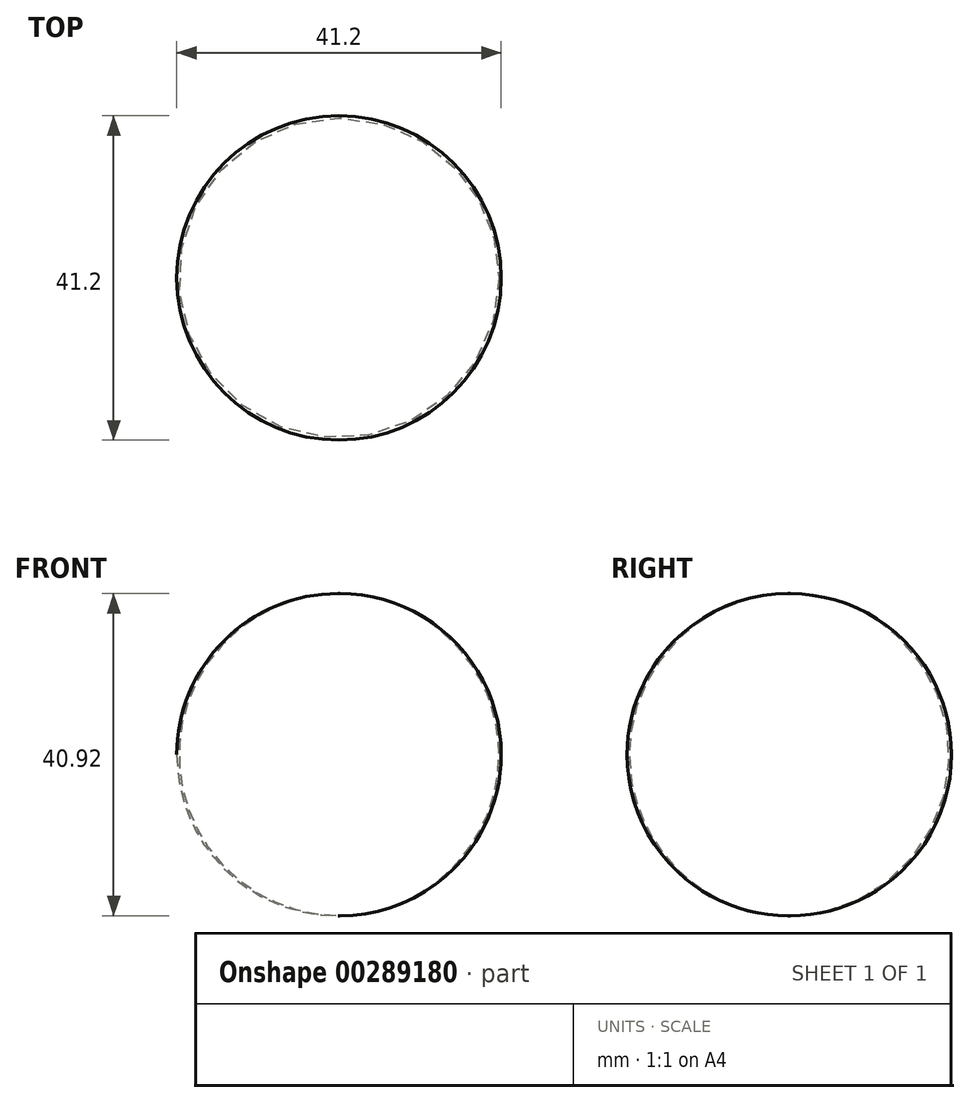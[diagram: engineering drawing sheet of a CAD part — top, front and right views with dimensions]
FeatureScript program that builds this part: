
annotation { "Feature Type Name" : "Feature", "Feature Type Description" : "" }
export const myFeature = defineFeature(function(context is Context, id is Id, definition is map)
    precondition{}
    {
        {
            var Q0;
            Q0=qCreatedBy(makeId("Front.planeOp"),FACE);
            var sketch = newSketch(context, id + "F0", { "sketchPlane" : qUnion([Q0])});
            skLineSegment(sketch, "E0", {"start": v(0, 0) * mm, "end": v(0, 40.92) * mm});
            skArc(sketch, "E1", {"start": v(0, 0) * mm, "mid": v(20.6, 20.46) * mm, "end": v(0, 40.92) * mm});
            skSolve(sketch);
        }
        {
            var Q0;
            Q0 = qSketchRegion(id + "F0", true);
            var Q1;
            Q1=sQuery(id+"F0.wireOp",EDGE,"E0");
            revolve(context, id + "F1", {"entities" : qUnion([Q0]), "axis" : qUnion([Q1]), "revolveType" : RevolveType.FULL});
        }
    });
